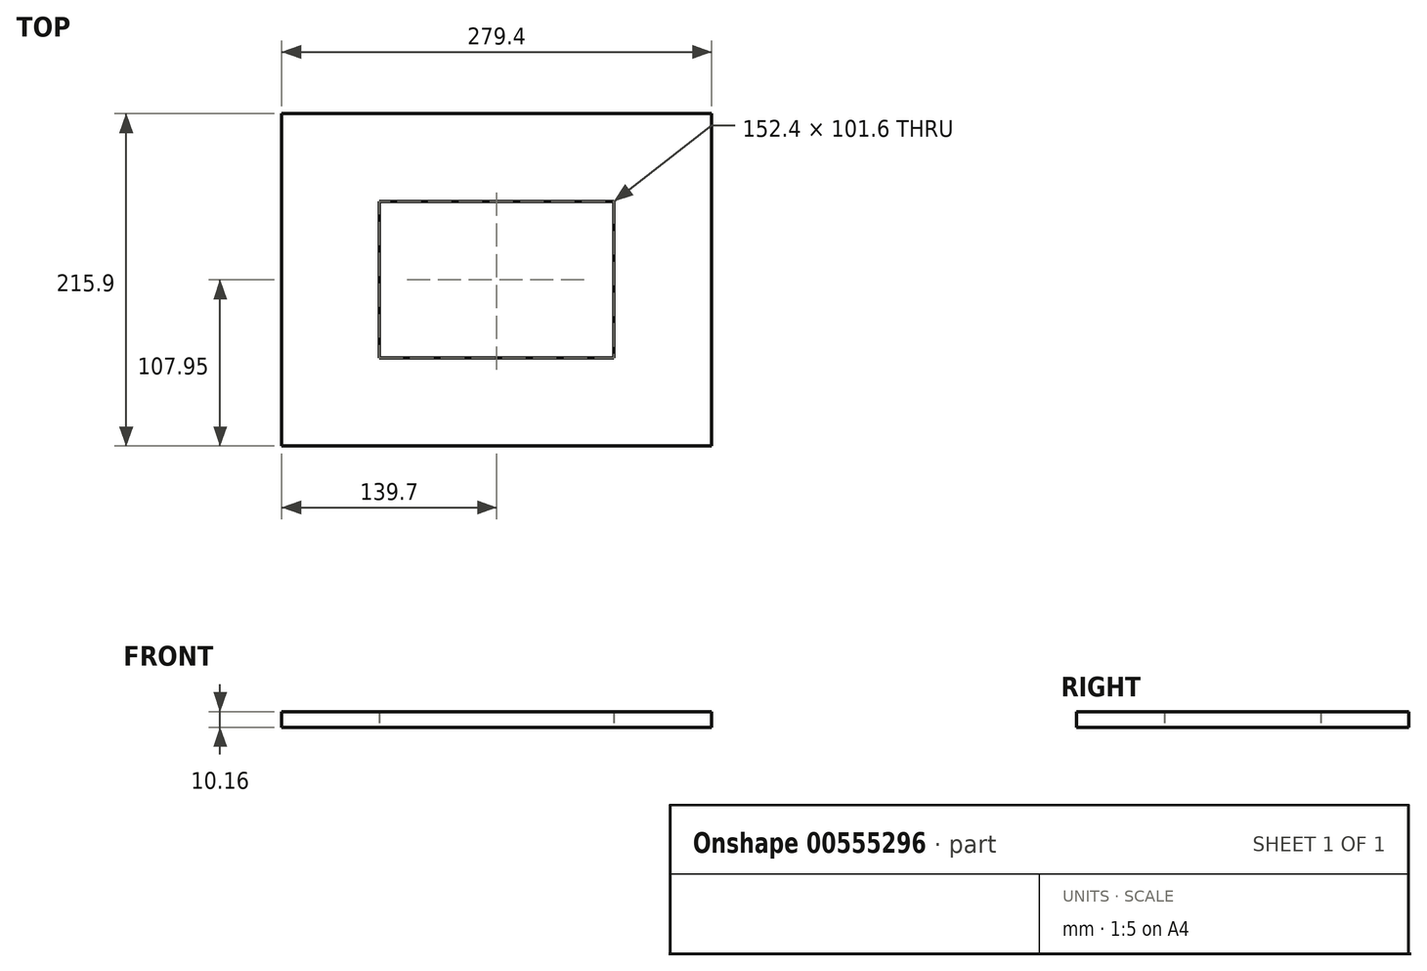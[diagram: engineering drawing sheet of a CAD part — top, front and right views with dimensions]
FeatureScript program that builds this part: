
annotation { "Feature Type Name" : "Feature", "Feature Type Description" : "" }
export const myFeature = defineFeature(function(context is Context, id is Id, definition is map)
    precondition{}
    {
        {
            var Q0;
            Q0=qCreatedBy(makeId("Top.planeOp"),FACE);
            var sketch = newSketch(context, id + "F0", { "sketchPlane" : qUnion([Q0])});
            skLineSegment(sketch, "E0.bottom", {"start": v(-139.7, 107.95) * mm, "end": v(139.7, 107.95) * mm});
            skLineSegment(sketch, "E0.top", {"start": v(-139.7, -107.95) * mm, "end": v(139.7, -107.95) * mm});
            skLineSegment(sketch, "E0.left", {"start": v(-139.7, 107.95) * mm, "end": v(-139.7, -107.95) * mm});
            skLineSegment(sketch, "E0.right", {"start": v(139.7, 107.95) * mm, "end": v(139.7, -107.95) * mm});
            skPoint(sketch, "E0.middle", {"position": v(0, 0) * mm});
            skLineSegment(sketch, "E1.bottom", {"start": v(-76.2, 50.8) * mm, "end": v(76.2, 50.8) * mm});
            skLineSegment(sketch, "E1.top", {"start": v(-76.2, -50.8) * mm, "end": v(76.2, -50.8) * mm});
            skLineSegment(sketch, "E1.left", {"start": v(-76.2, 50.8) * mm, "end": v(-76.2, -50.8) * mm});
            skLineSegment(sketch, "E1.right", {"start": v(76.2, 50.8) * mm, "end": v(76.2, -50.8) * mm});
            skSolve(sketch);
        }
        {
            var Q0;
            Q0=makeQuery(id+"F0.imprint","IMPRINT",FACE,{"disambiguationData":[TD([[makeQuery(id+"F0.imprint","IMPRINT",EDGE,{"derivedFrom":sQuery(id+"F0.wireOp",EDGE,"E0.bottom")}),-1.0]])]});
            extrude(context, id + "F1", {"entities" : qUnion([Q0]), "endBound" : BoundingType.SYMMETRIC, "depth" : 10.16 * mm, "offsetDistance" : 25.4 * mm});
        }
    });
